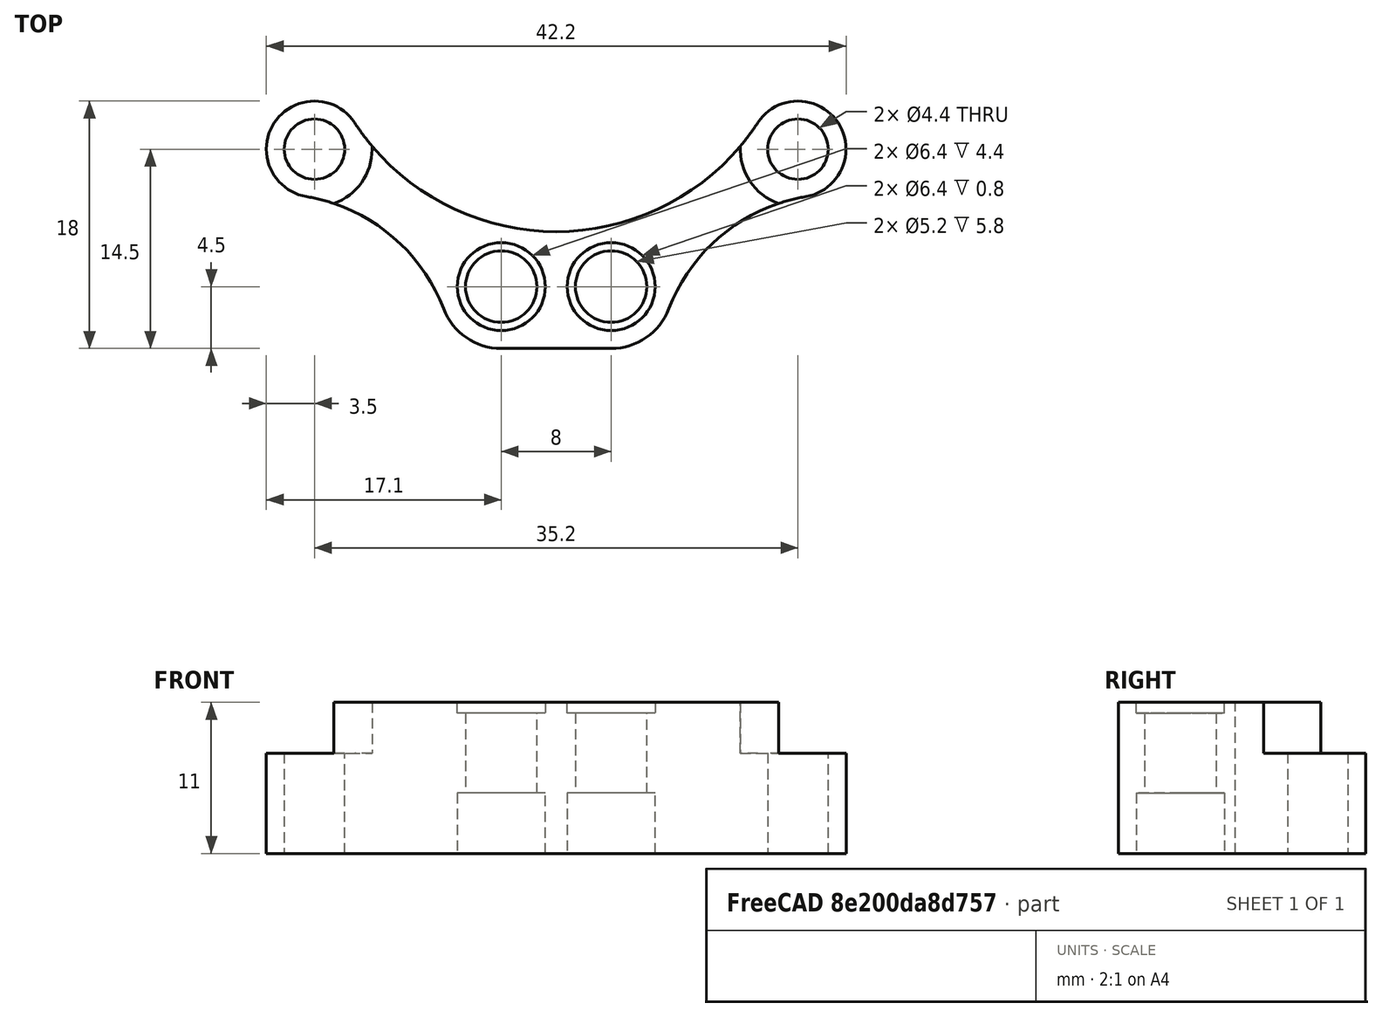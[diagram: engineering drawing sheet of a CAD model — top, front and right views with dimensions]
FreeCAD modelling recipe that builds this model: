
FCSTD DOCUMENT  (FreeCAD 0.18R4 (GitTag))
Label: Stepper_Motor_Mount
License: All rights reserved
LicenseURL: http://en.wikipedia.org/wiki/All_rights_reserved
objects: Sketcher::SketchObject×6, PartDesign::Pocket×3, PartDesign::Pad×1, PartDesign::Body×1, Mesh::Feature×1
note: 15 computed .brp shape members not serialized (recipe doc carries the construction recipe); baked Part::Feature solids carry a one-line shape summary decoded from their .brp

FEATURE [Sketcher::SketchObject] Sketch
  MapMode = 5
  Support = -> [XY_Plane]
  sketch-geometry (8):
    g0: Circle [constr] CenterX=0 CenterY=8 CenterZ=0 NormalX=0 NormalY=0 NormalZ=1 AngleXU=0 Radius=14
    g1: Circle CenterX=4 CenterY=-10 CenterZ=0 NormalX=0 NormalY=0 NormalZ=1 AngleXU=0 Radius=2.6
    g2: Circle CenterX=17.6 CenterY=0 CenterZ=0 NormalX=0 NormalY=0 NormalZ=1 AngleXU=0 Radius=2.2
    g3: LineSegment StartX=4 StartY=-14.5 StartZ=0 EndX=0 EndY=-14.5 EndZ=0
    g4: ArcOfCircle CenterX=4 CenterY=-10 CenterZ=0 NormalX=0 NormalY=0 NormalZ=1 AngleXU=0 Radius=4.5 StartAngle=4.71239 EndAngle=5.91668
    g5: ArcOfCircle CenterX=17.6 CenterY=0 CenterZ=0 NormalX=0 NormalY=0 NormalZ=1 AngleXU=0 Radius=3.5 StartAngle=4.87908 EndAngle=8.8439
    g6: ArcOfCircle CenterX=20.3377 CenterY=-16.2713 CenterZ=0 NormalX=0 NormalY=0 NormalZ=1 AngleXU=0 Radius=13 StartAngle=1.73749 EndAngle=2.77508
    g7: ArcOfCircle CenterX=0 CenterY=11.5532 CenterZ=0 NormalX=0 NormalY=0 NormalZ=1 AngleXU=0 Radius=17.5532 StartAngle=4.71239 EndAngle=5.7023
  constraints (24):
    c: Radius(g0) = 14
    c: PointOnObject(g0,g-2)
    c: DistanceY(g-1,g0) = 8
    c: Radius(g1) = 2.6
    c: DistanceX(g-1,g1) = 4
    c: Radius(g2) = 2.2
    c: PointOnObject(g2,g-1)
    c: DistanceX(g-1,g2) = 17.6
    c: PointOnObject(g3,g-2)
    c: Horizontal(g3)
    c: Vertical(g1,g3)
    c: Coincident(g4,g1)
    c: DistanceY(g1,g-1) = 10
    c: Radius(g4) = 4.5
    c: Coincident(g5,g2)
    c: Radius(g5) = 3.5
    c: Radius(g6) = 13
    c: PointOnObject(g7,g-2)
    c: PointOnObject(g7,g0)
    c: PointOnObject(g7,g-2)
    c: Tangent(g6,g4) = 1.5708
    c: Tangent(g5,g6) = 1.5708
    c: Tangent(g7,g5) = 1.5708
    c: Coincident(g3,g4)
FEATURE [Sketcher::SketchObject] MirroredSketch
  sketch-geometry (8):
    g0: Circle [constr] CenterX=0 CenterY=8 CenterZ=0 NormalX=0 NormalY=0 NormalZ=1 AngleXU=0 Radius=14
    g1: Circle CenterX=-4 CenterY=-10 CenterZ=0 NormalX=0 NormalY=0 NormalZ=1 AngleXU=0 Radius=2.6
    g2: Circle CenterX=-17.6 CenterY=0 CenterZ=0 NormalX=0 NormalY=0 NormalZ=1 AngleXU=0 Radius=2.2
    g3: LineSegment StartX=-4 StartY=-14.5 StartZ=0 EndX=0 EndY=-14.5 EndZ=0
    g4: ArcOfCircle CenterX=-4 CenterY=-10 CenterZ=0 NormalX=0 NormalY=0 NormalZ=1 AngleXU=0 Radius=4.5 StartAngle=3.5081 EndAngle=4.71239
    g5: ArcOfCircle CenterX=-17.6 CenterY=0 CenterZ=0 NormalX=0 NormalY=0 NormalZ=1 AngleXU=0 Radius=3.5 StartAngle=0.580882 EndAngle=4.5457
    g6: ArcOfCircle CenterX=-20.3377 CenterY=-16.2713 CenterZ=0 NormalX=0 NormalY=0 NormalZ=1 AngleXU=0 Radius=13 StartAngle=0.36651 EndAngle=1.4041
    g7: ArcOfCircle CenterX=0 CenterY=11.5532 CenterZ=0 NormalX=0 NormalY=0 NormalZ=1 AngleXU=0 Radius=17.5532 StartAngle=3.72247 EndAngle=4.71239
  constraints (14):
    c: Radius(g0) = 14
    c: Radius(g1) = 2.6
    c: Radius(g2) = 2.2
    c: Horizontal(g3)
    c: Coincident(g4,g1)
    c: Radius(g4) = 4.5
    c: Coincident(g5,g2)
    c: Radius(g5) = 3.5
    c: Radius(g6) = 13
    c: PointOnObject(g7,g0)
    c: Tangent(g6,g4) = 1.5708
    c: Tangent(g5,g6) = 1.5708
    c: Tangent(g7,g5) = 1.5708
    c: Coincident(g3,g4)
FEATURE [Sketcher::SketchObject] Sketch001
  sketch-geometry (16):
    g0: Circle [constr] CenterX=0 CenterY=8 CenterZ=0 NormalX=0 NormalY=0 NormalZ=1 AngleXU=0 Radius=14
    g1: Circle CenterX=-4 CenterY=-10 CenterZ=0 NormalX=0 NormalY=0 NormalZ=1 AngleXU=0 Radius=2.6
    g2: Circle CenterX=-17.6 CenterY=0 CenterZ=0 NormalX=0 NormalY=0 NormalZ=1 AngleXU=0 Radius=2.2
    g3: LineSegment StartX=-4 StartY=-14.5 StartZ=0 EndX=0 EndY=-14.5 EndZ=0
    g4: ArcOfCircle CenterX=-4 CenterY=-10 CenterZ=0 NormalX=0 NormalY=0 NormalZ=1 AngleXU=0 Radius=4.5 StartAngle=3.5081 EndAngle=4.71239
    g5: ArcOfCircle CenterX=-17.6 CenterY=0 CenterZ=0 NormalX=0 NormalY=0 NormalZ=1 AngleXU=0 Radius=3.5 StartAngle=0.580882 EndAngle=4.5457
    g6: ArcOfCircle CenterX=-20.3377 CenterY=-16.2713 CenterZ=0 NormalX=0 NormalY=0 NormalZ=1 AngleXU=0 Radius=13 StartAngle=0.36651 EndAngle=1.4041
    g7: ArcOfCircle CenterX=0 CenterY=11.5532 CenterZ=0 NormalX=0 NormalY=0 NormalZ=1 AngleXU=0 Radius=17.5532 StartAngle=3.72247 EndAngle=4.71239
    g8: Circle [constr] CenterX=0 CenterY=8 CenterZ=0 NormalX=0 NormalY=0 NormalZ=1 AngleXU=0 Radius=14
    g9: Circle CenterX=4 CenterY=-10 CenterZ=0 NormalX=0 NormalY=0 NormalZ=1 AngleXU=0 Radius=2.6
    g10: Circle CenterX=17.6 CenterY=0 CenterZ=0 NormalX=0 NormalY=0 NormalZ=1 AngleXU=0 Radius=2.2
    g11: LineSegment StartX=4 StartY=-14.5 StartZ=0 EndX=0 EndY=-14.5 EndZ=0
    g12: ArcOfCircle CenterX=4 CenterY=-10 CenterZ=0 NormalX=0 NormalY=0 NormalZ=1 AngleXU=0 Radius=4.5 StartAngle=4.71239 EndAngle=5.91668
    g13: ArcOfCircle CenterX=17.6 CenterY=0 CenterZ=0 NormalX=0 NormalY=0 NormalZ=1 AngleXU=0 Radius=3.5 StartAngle=4.87908 EndAngle=8.8439
    g14: ArcOfCircle CenterX=20.3377 CenterY=-16.2713 CenterZ=0 NormalX=0 NormalY=0 NormalZ=1 AngleXU=0 Radius=13 StartAngle=1.73749 EndAngle=2.77508
    g15: ArcOfCircle CenterX=0 CenterY=11.5532 CenterZ=0 NormalX=0 NormalY=0 NormalZ=1 AngleXU=0 Radius=17.5532 StartAngle=4.71239 EndAngle=5.7023
  constraints (38):
    c: Radius(g0) = 14
    c: Radius(g1) = 2.6
    c: Radius(g2) = 2.2
    c: Horizontal(g3)
    c: Coincident(g4,g1)
    c: Radius(g4) = 4.5
    c: Coincident(g5,g2)
    c: Radius(g5) = 3.5
    c: Radius(g6) = 13
    c: PointOnObject(g7,g0)
    c: Tangent(g6,g4) = 1.5708
    c: Tangent(g5,g6) = 1.5708
    c: Tangent(g7,g5) = 1.5708
    c: Coincident(g3,g4)
    c: Radius(g8) = 14
    c: PointOnObject(g8,g-2)
    c: DistanceY(g-1,g8) = 8
    c: Radius(g9) = 2.6
    c: DistanceX(g-1,g9) = 4
    c: Radius(g10) = 2.2
    c: PointOnObject(g10,g-1)
    c: DistanceX(g-1,g10) = 17.6
    c: PointOnObject(g11,g-2)
    c: Horizontal(g11)
    c: Vertical(g9,g11)
    c: Coincident(g12,g9)
    c: DistanceY(g9,g-1) = 10
    c: Radius(g12) = 4.5
    c: Coincident(g13,g10)
    c: Radius(g13) = 3.5
    c: Radius(g14) = 13
    c: PointOnObject(g15,g-2)
    c: PointOnObject(g15,g8)
    c: PointOnObject(g15,g-2)
    c: Tangent(g14,g12) = 1.5708
    c: Tangent(g13,g14) = 1.5708
    c: Tangent(g15,g13) = 1.5708
    c: Coincident(g11,g12)
FEATURE [PartDesign::Pad] Pad
  Length = 11
  Length2 = 100
  Profile = -> Sketch001
  Type = 0
FEATURE [Sketcher::SketchObject] Sketch003
  MapMode = 5
  Placement = pos=(0,0,11) rot=(0,0,1;0rad)
  sketch-geometry (2):
    g0: Circle CenterX=-17.6 CenterY=0 CenterZ=0 NormalX=0 NormalY=0 NormalZ=1 AngleXU=0 Radius=4.2
    g1: Circle CenterX=17.6 CenterY=0 CenterZ=0 NormalX=0 NormalY=0 NormalZ=1 AngleXU=0 Radius=4.2
  constraints (2):
    c: Equal(g0,g1)
    c: Radius(g1) = 4.2
FEATURE [PartDesign::Pocket] Pocket001
  BaseFeature = -> Pad
  Length = 3.7
  Length2 = 100
  Profile = -> Sketch003
  Type = 0
FEATURE [Sketcher::SketchObject] Sketch004
  ExternalGeometry = -> [Pocket001]
  MapMode = 5
  Placement = pos=(0,0,0) rot=(1,0,0;3.14159rad)
  Support = -> [Pocket001]
  sketch-geometry (2):
    g0: Circle CenterX=-4 CenterY=10 CenterZ=0 NormalX=0 NormalY=0 NormalZ=1 AngleXU=0 Radius=3.2
    g1: Circle CenterX=4 CenterY=10 CenterZ=0 NormalX=0 NormalY=0 NormalZ=1 AngleXU=0 Radius=3.2
  constraints (4):
    c: Coincident(g1,g-4)
    c: Coincident(g0,g-3)
    c: Equal(g0,g1)
    c: Radius(g1) = 3.2
FEATURE [PartDesign::Pocket] Pocket
  BaseFeature = -> Pocket001
  Length = 4.4
  Length2 = 100
  Profile = -> Sketch004
  Type = 0
FEATURE [Sketcher::SketchObject] Sketch005
  ExternalGeometry = -> [Pocket]
  MapMode = 5
  Placement = pos=(0,0,11) rot=(0,0,1;0rad)
  Support = -> [Pocket]
  sketch-geometry (2):
    g0: Circle CenterX=-4 CenterY=-10 CenterZ=0 NormalX=0 NormalY=0 NormalZ=1 AngleXU=0 Radius=3.2
    g1: Circle CenterX=4 CenterY=-10 CenterZ=0 NormalX=0 NormalY=0 NormalZ=1 AngleXU=0 Radius=3.2
  constraints (4):
    c: Coincident(g1,g-4)
    c: Coincident(g0,g-3)
    c: Equal(g0,g1)
    c: Radius(g1) = 3.2
FEATURE [PartDesign::Pocket] Pocket002
  BaseFeature = -> Pocket
  Length = 0.8
  Length2 = 100
  Profile = -> Sketch005
  Type = 0
FEATURE [PartDesign::Body] Body
  Group = -> [Sketch,MirroredSketch,Sketch001,Pad,Sketch003,Pocket001,Sketch004,Pocket,Sketch005,Pocket002]
  Origin = -> Origin
  Tip = -> Pocket002
FEATURE [Mesh::Feature] Mesh  label="Pocket002 (Meshed)"
